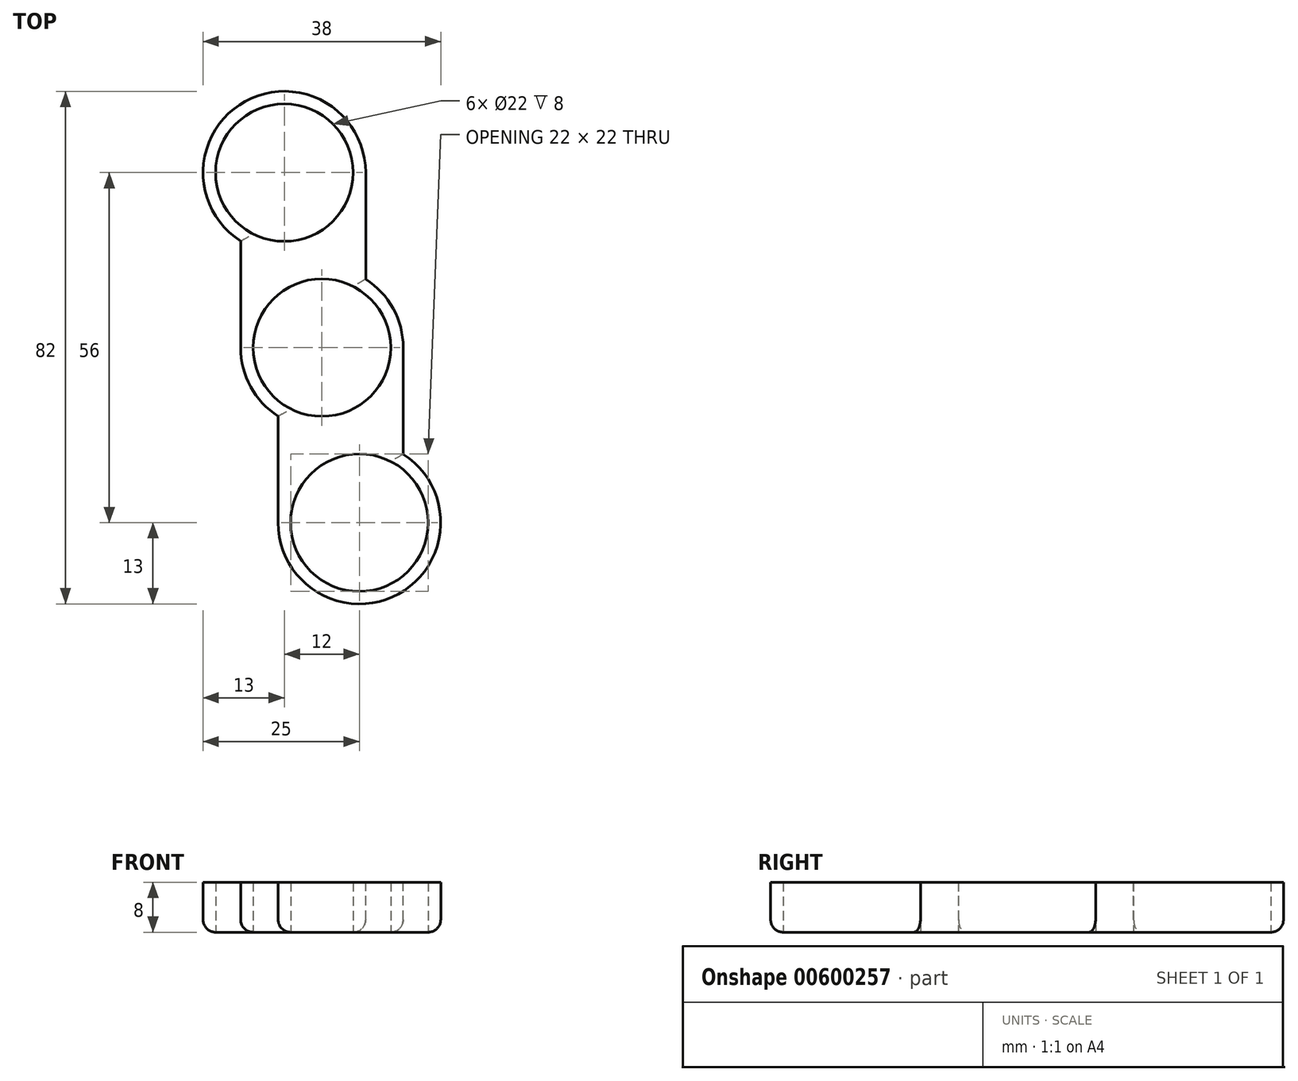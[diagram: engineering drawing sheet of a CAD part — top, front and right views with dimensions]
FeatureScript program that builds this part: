
annotation { "Feature Type Name" : "Feature", "Feature Type Description" : "" }
export const myFeature = defineFeature(function(context is Context, id is Id, definition is map)
    precondition{}
    {
        {
            var Q0;
            Q0=qCreatedBy(makeId("Top.planeOp"),FACE);
            var sketch = newSketch(context, id + "F0", { "sketchPlane" : qUnion([Q0])});
            skCircle(sketch, "E0", {"center": v(0, 0) * mm, "radius": 11 * mm});
            skCircle(sketch, "E1", {"center": v(-6, 28) * mm, "radius": 11 * mm});
            skLineSegment(sketch, "E2.bottom", {"start": v(20, -42) * mm, "end": v(-20, -42) * mm});
            skLineSegment(sketch, "E2.top", {"start": v(20, 42) * mm, "end": v(-20, 42) * mm});
            skLineSegment(sketch, "E2.left", {"start": v(20, -42) * mm, "end": v(20, 42) * mm});
            skLineSegment(sketch, "E2.right", {"start": v(-20, -42) * mm, "end": v(-20, 42) * mm});
            skPoint(sketch, "E3", {"position": v(0, 42) * mm});
            skPoint(sketch, "E4", {"position": v(-20, 0) * mm});
            skPoint(sketch, "E5", {"position": v(20, 0) * mm});
            skPoint(sketch, "E6", {"position": v(0, -42) * mm});
            skPoint(sketch, "E7", {"position": v(-20, -21) * mm});
            skPoint(sketch, "E8", {"position": v(-20, 21) * mm});
            skPoint(sketch, "E9", {"position": v(0, 28) * mm});
            skPoint(sketch, "E10", {"position": v(0, -28) * mm});
            skPoint(sketch, "E11", {"position": v(6, -28) * mm});
            skCircle(sketch, "E12", {"center": v(6, -28) * mm, "radius": 11 * mm});
            skPoint(sketch, "E13.MirrorP", {"position": v(20, -21) * mm});
            skPoint(sketch, "E14.MirrorP", {"position": v(20, 21) * mm});
            skPoint(sketch, "E15", {"position": v(-16.5, 0) * mm});
            skPoint(sketch, "E16", {"position": v(16.5, 0) * mm});
            skSolve(sketch);
        }
        {
            var Q0;
            Q0=makeQuery(id+"F0.imprint","IMPRINT",FACE,{"disambiguationData":[TD([[makeQuery(id+"F0.imprint","IMPRINT",EDGE,{"derivedFrom":sQuery(id+"F0.wireOp",EDGE,"E0")}),-1.0]])]});
            extrude(context, id + "F1", {"entities" : qUnion([Q0]), "depth" : 4 * mm, "offsetDistance" : 25 * mm, "hasSecondDirection" : true, "secondDirectionOppositeDirection" : true, "secondDirectionDepth" : 4 * mm});
        }
        {
            var Q0;
            Q0=makeQuery(id+"F1.opExtrude","CAP_FACE",FACE,{"disambiguationData":[OSD([sQuery(id+"F0.wireOp",EDGE,"E0"),sQuery(id+"F0.wireOp",EDGE,"E1"),sQuery(id+"F0.wireOp",EDGE,"E2.bottom"),sQuery(id+"F0.wireOp",EDGE,"E2.top"),sQuery(id+"F0.wireOp",EDGE,"E2.left"),sQuery(id+"F0.wireOp",EDGE,"E2.right"),sQuery(id+"F0.wireOp",EDGE,"E12")])],"isStart":false});
            var sketch = newSketch(context, id + "F2", { "sketchPlane" : qUnion([Q0])});
            skPoint(sketch, "E17", {"position": v(0, 0) * mm});
            skPoint(sketch, "E18", {"position": v(-20, 42) * mm});
            skPoint(sketch, "E19", {"position": v(20, -42) * mm});
            skCircle(sketch, "E20", {"center": v(0, 0) * mm, "radius": 13 * mm});
            skLineSegment(sketch, "E21.bottom", {"start": v(-20, 42) * mm, "end": v(20, 42) * mm});
            skLineSegment(sketch, "E21.top", {"start": v(-20, -42) * mm, "end": v(20, -42) * mm});
            skLineSegment(sketch, "E21.left", {"start": v(-20, 42) * mm, "end": v(-20, -42) * mm});
            skLineSegment(sketch, "E21.right", {"start": v(20, 42) * mm, "end": v(20, -42) * mm});
            skPoint(sketch, "E22", {"position": v(-6, 28) * mm});
            skPoint(sketch, "E23", {"position": v(6, -28) * mm});
            skCircle(sketch, "E24", {"center": v(-6, 28) * mm, "radius": 13 * mm});
            skCircle(sketch, "E25", {"center": v(6, -28) * mm, "radius": 13 * mm});
            skPoint(sketch, "E26", {"position": v(13, 0) * mm});
            skPoint(sketch, "E27", {"position": v(7, 28) * mm});
            skPoint(sketch, "E28", {"position": v(-19, 28) * mm});
            skPoint(sketch, "E29", {"position": v(-13, 0) * mm});
            skPoint(sketch, "E30", {"position": v(19, -28) * mm});
            skPoint(sketch, "E31", {"position": v(-7, -28) * mm});
            skLineSegment(sketch, "E32", {"start": v(13, 0) * mm, "end": v(13, -17.05) * mm});
            skLineSegment(sketch, "E33", {"start": v(7, 28) * mm, "end": v(7, 10.95) * mm});
            skLineSegment(sketch, "E34", {"start": v(-7, -28) * mm, "end": v(-7, -10.95) * mm});
            skLineSegment(sketch, "E35", {"start": v(-13, 0) * mm, "end": v(-13, 17.05) * mm});
            skSolve(sketch);
        }
        {
            var Q0;
            Q0=makeQuery(id+"F2.imprint","IMPRINT",FACE,{"disambiguationData":[TD([[makeQuery(id+"F2.imprint","IMPRINT",EDGE,{"derivedFrom":sQuery(id+"F2.wireOp",EDGE,"E21.bottom")}),1.0]])]});
            extrude(context, id + "F3", {"entities" : qUnion([Q0]), "operationType" : NewBodyOperationType.REMOVE, "oppositeDirection" : true, "depth" : 25 * mm, "offsetDistance" : 25 * mm});
        }
        {
            var Q0;
            Q0=makeQuery(id+"F3.boolean.opBoolean","COPY",EDGE,{"derivedFrom":makeQuery(id+"F3.opExtrude","CAP_EDGE",EDGE,{"disambiguationData":[OSD([sQuery(id+"F2.wireOp",EDGE,"E24")])],"isStart":true})});
            var Q1;
            Q1=makeQuery(id+"F3.boolean.opBoolean","COPY",EDGE,{"derivedFrom":makeQuery(id+"F3.opExtrude","CAP_EDGE",EDGE,{"disambiguationData":[OSD([sQuery(id+"F2.wireOp",EDGE,"E34")])],"isStart":true})});
            var Q2;
            Q2=makeQuery(id+"F3.boolean.opBoolean","INTERSECT",EDGE,{"derivedFrom":[makeQuery(id+"F1.opExtrude","CAP_FACE",FACE,{"disambiguationData":[OSD([sQuery(id+"F0.wireOp",EDGE,"E0"),sQuery(id+"F0.wireOp",EDGE,"E1"),sQuery(id+"F0.wireOp",EDGE,"E2.bottom"),sQuery(id+"F0.wireOp",EDGE,"E2.top"),sQuery(id+"F0.wireOp",EDGE,"E2.left"),sQuery(id+"F0.wireOp",EDGE,"E2.right"),sQuery(id+"F0.wireOp",EDGE,"E12")])],"isStart":true}),makeQuery(id+"F3.opExtrude","SWEPT_FACE",FACE,{"disambiguationData":[OSD([sQuery(id+"F2.wireOp",EDGE,"E34")])]})]});
            var Q3;
            Q3=makeQuery(id+"F3.boolean.opBoolean","INTERSECT",EDGE,{"derivedFrom":[makeQuery(id+"F1.opExtrude","CAP_FACE",FACE,{"disambiguationData":[OSD([sQuery(id+"F0.wireOp",EDGE,"E0"),sQuery(id+"F0.wireOp",EDGE,"E1"),sQuery(id+"F0.wireOp",EDGE,"E2.bottom"),sQuery(id+"F0.wireOp",EDGE,"E2.top"),sQuery(id+"F0.wireOp",EDGE,"E2.left"),sQuery(id+"F0.wireOp",EDGE,"E2.right"),sQuery(id+"F0.wireOp",EDGE,"E12")])],"isStart":true}),makeQuery(id+"F3.opExtrude","SWEPT_FACE",FACE,{"disambiguationData":[OSD([sQuery(id+"F2.wireOp",EDGE,"E33")])]})]});
            fillet(context, id + "F4", {"entities" : qUnion([Q0, Q1, Q2, Q3]), "radius" : 2 * mm, "tangentPropagation" : true, "allowEdgeOverflow" : false});
        }
        {
            var Q0;
            Q0=makeQuery(id+"F3.boolean.opBoolean","INTERSECT",EDGE,{"derivedFrom":[makeQuery(id+"F1.opExtrude","CAP_FACE",FACE,{"disambiguationData":[OSD([sQuery(id+"F0.wireOp",EDGE,"E0"),sQuery(id+"F0.wireOp",EDGE,"E1"),sQuery(id+"F0.wireOp",EDGE,"E2.bottom"),sQuery(id+"F0.wireOp",EDGE,"E2.top"),sQuery(id+"F0.wireOp",EDGE,"E2.left"),sQuery(id+"F0.wireOp",EDGE,"E2.right"),sQuery(id+"F0.wireOp",EDGE,"E12")])],"isStart":true}),makeQuery(id+"F3.opExtrude","SWEPT_FACE",FACE,{"disambiguationData":[OSD([sQuery(id+"F2.wireOp",EDGE,"E35")])]})]});
            var Q1;
            Q1=makeQuery(id+"F3.boolean.opBoolean","INTERSECT",EDGE,{"derivedFrom":[makeQuery(id+"F1.opExtrude","CAP_FACE",FACE,{"disambiguationData":[OSD([sQuery(id+"F0.wireOp",EDGE,"E0"),sQuery(id+"F0.wireOp",EDGE,"E1"),sQuery(id+"F0.wireOp",EDGE,"E2.bottom"),sQuery(id+"F0.wireOp",EDGE,"E2.top"),sQuery(id+"F0.wireOp",EDGE,"E2.left"),sQuery(id+"F0.wireOp",EDGE,"E2.right"),sQuery(id+"F0.wireOp",EDGE,"E12")])],"isStart":true}),makeQuery(id+"F3.opExtrude","SWEPT_FACE",FACE,{"disambiguationData":[OSD([sQuery(id+"F2.wireOp",EDGE,"E32")])]})]});
            var Q2;
            Q2=makeQuery(id+"F3.boolean.opBoolean","COPY",EDGE,{"derivedFrom":makeQuery(id+"F3.opExtrude","CAP_EDGE",EDGE,{"disambiguationData":[OSD([sQuery(id+"F2.wireOp",EDGE,"E32")])],"isStart":true})});
            var Q3;
            Q3=makeQuery(id+"F3.boolean.opBoolean","COPY",EDGE,{"derivedFrom":makeQuery(id+"F3.opExtrude","CAP_EDGE",EDGE,{"disambiguationData":[OSD([sQuery(id+"F2.wireOp",EDGE,"E35")])],"isStart":true})});
            fillet(context, id + "F5", {"entities" : qUnion([Q0, Q1, Q2, Q3]), "radius" : 2 * mm, "tangentPropagation" : true, "allowEdgeOverflow" : false});
        }
    });
